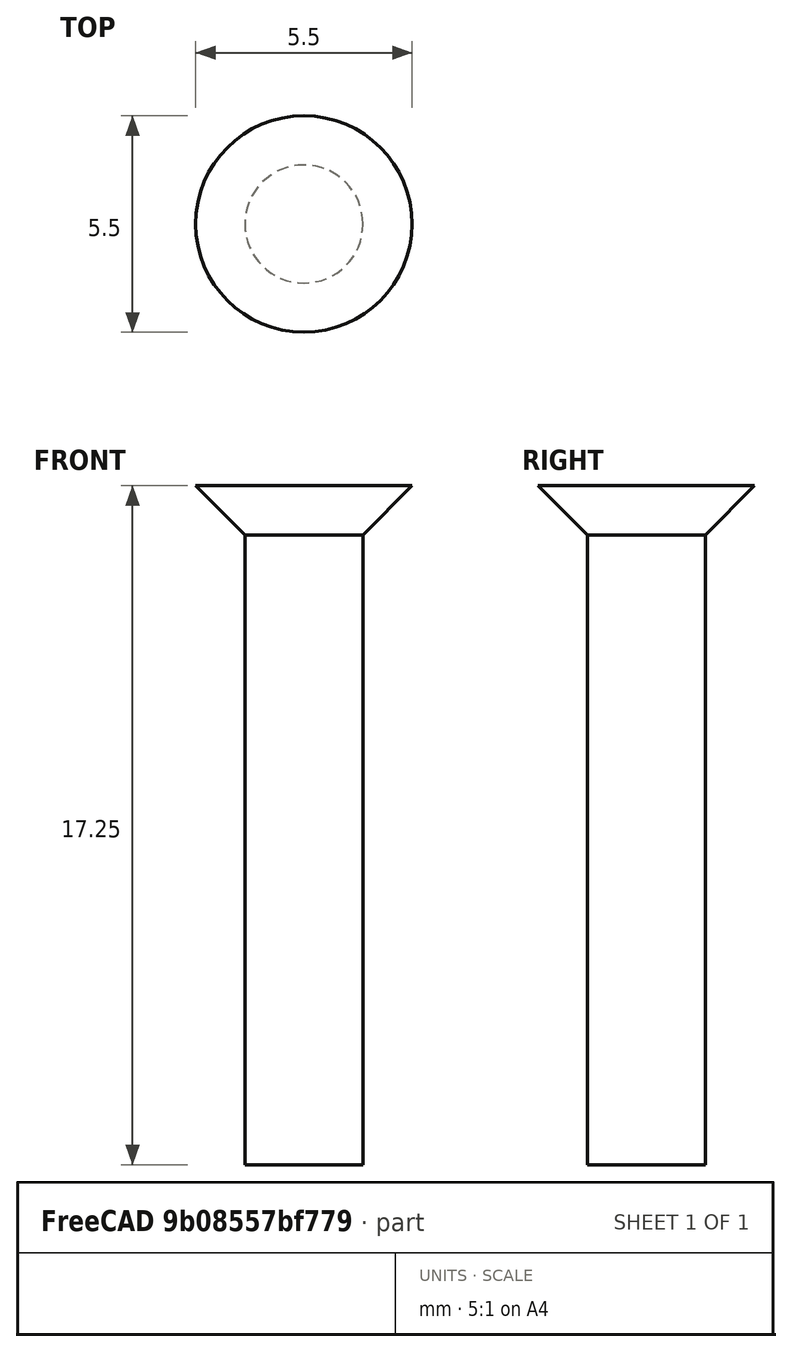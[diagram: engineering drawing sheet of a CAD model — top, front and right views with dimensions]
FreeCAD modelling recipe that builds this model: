
FCSTD DOCUMENT  (FreeCAD 0.18R14555 (Git shallow))
Label: m3-16
License: All rights reserved
LicenseURL: http://en.wikipedia.org/wiki/All_rights_reserved
objects: Sketcher::SketchObject×1, PartDesign::Revolution×1, PartDesign::Body×1
note: 4 computed .brp shape members not serialized (recipe doc carries the construction recipe); baked Part::Feature solids carry a one-line shape summary decoded from their .brp

FEATURE [Sketcher::SketchObject] Sketch
  MapMode = 5
  Placement = pos=(0,0,0) rot=(1,0,0;1.5708rad)
  Support = -> [XZ_Plane]
  sketch-geometry (5):
    g0: LineSegment StartX=0 StartY=0 StartZ=0 EndX=1.5 EndY=0 EndZ=0
    g1: LineSegment StartX=1.5 StartY=0 StartZ=0 EndX=1.5 EndY=16 EndZ=0
    g2: LineSegment StartX=1.5 StartY=16 StartZ=0 EndX=2.75 EndY=17.25 EndZ=0
    g3: LineSegment StartX=2.75 StartY=17.25 StartZ=0 EndX=0 EndY=17.25 EndZ=0
    g4: LineSegment StartX=0 StartY=17.25 StartZ=0 EndX=0 EndY=0 EndZ=0
  constraints (14):
    c: Horizontal(g0)
    c: Coincident(g0,g1)
    c: Vertical(g1)
    c: Coincident(g1,g2)
    c: Coincident(g2,g3)
    c: Horizontal(g3)
    c: Coincident(g3,g4)
    c: Vertical(g4)
    c: Coincident(g4,g0)
    c: Coincident(g0,g-1)
    c: DistanceX(g0,g0) = 1.5
    c: DistanceY(g1,g1) = 16
    c: DistanceX(g3,g3) = 2.75
    c: Angle(g1,g2) = 2.35619
FEATURE [PartDesign::Revolution] Revolution
  Angle = 360
  Axis = (0,2e-16,1)
  Base = (0,0,0)
  Placement = pos=(0,0,0) rot=(1,0,0;1.5708rad)
  Profile = -> Sketch
  ReferenceAxis = -> Sketch [V_Axis]
  Reversed = true
FEATURE [PartDesign::Body] Body
  Group = -> [Sketch,Revolution]
  Origin = -> Origin
  Tip = -> Revolution
